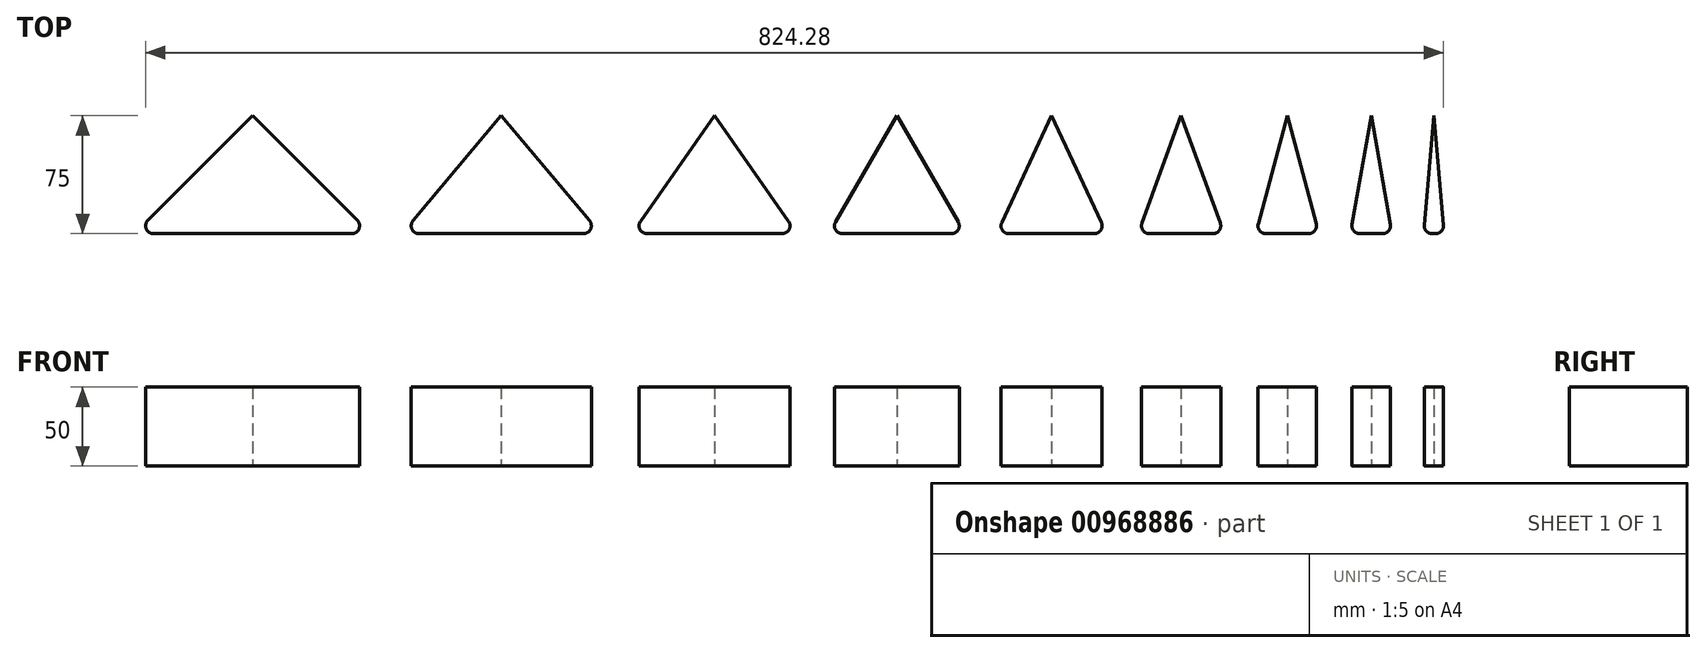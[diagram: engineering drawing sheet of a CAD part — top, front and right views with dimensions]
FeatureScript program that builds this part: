
annotation { "Feature Type Name" : "Feature", "Feature Type Description" : "" }
export const myFeature = defineFeature(function(context is Context, id is Id, definition is map)
    precondition{}
    {
        {
            var Q0;
            Q0=qCreatedBy(makeId("Top.planeOp"),FACE);
            var sketch = newSketch(context, id + "F0", { "sketchPlane" : qUnion([Q0])});
            skLineSegment(sketch, "E0", {"start": v(-473.41, 0) * mm, "end": v(499.22, 0) * mm});
            skLineSegment(sketch, "E1", {"start": v(-389.99, 0) * mm, "end": v(-389.99, 75) * mm});
            skLineSegment(sketch, "E2", {"start": v(-389.99, 75) * mm, "end": v(-464.99, 0) * mm});
            skLineSegment(sketch, "E3.MirrorCS", {"start": v(-389.99, 75) * mm, "end": v(-314.99, 0) * mm});
            skLineSegment(sketch, "E4", {"start": v(-473.41, 0) * mm, "end": v(-473.41, 75) * mm});
            skLineSegment(sketch, "E5", {"start": v(-473.41, 75) * mm, "end": v(499.22, 75) * mm});
            skLineSegment(sketch, "E6", {"start": v(499.22, 75) * mm, "end": v(499.22, 0) * mm});
            skLineSegment(sketch, "E7", {"start": v(-294.99, 0) * mm, "end": v(-232.05, 75) * mm});
            skLineSegment(sketch, "E8", {"start": v(-232.05, 75) * mm, "end": v(-232.05, 0) * mm});
            skLineSegment(sketch, "E9.MirrorCS", {"start": v(-169.12, 0) * mm, "end": v(-232.05, 75) * mm});
            skLineSegment(sketch, "E10", {"start": v(-149.12, 0) * mm, "end": v(-96.6, 75) * mm});
            skLineSegment(sketch, "E11", {"start": v(-96.6, 75) * mm, "end": v(-96.6, 0) * mm});
            skLineSegment(sketch, "E12", {"start": v(-314.99, 0) * mm, "end": v(-294.99, 0) * mm});
            skLineSegment(sketch, "E13", {"start": v(-169.12, 0) * mm, "end": v(-149.12, 0) * mm});
            skLineSegment(sketch, "E14.MirrorCS", {"start": v(-44.1, 0) * mm, "end": v(-96.6, 75) * mm});
            skLineSegment(sketch, "E15", {"start": v(-44.1, 0) * mm, "end": v(-24.1, 0) * mm});
            skLineSegment(sketch, "E16", {"start": v(-24.1, 0) * mm, "end": v(19.21, 75) * mm});
            skLineSegment(sketch, "E17", {"start": v(19.21, 75) * mm, "end": v(19.21, 0) * mm});
            skLineSegment(sketch, "E18.MirrorCS", {"start": v(62.51, 0) * mm, "end": v(19.21, 75) * mm});
            skLineSegment(sketch, "E19", {"start": v(62.51, 0) * mm, "end": v(82.51, 0) * mm});
            skLineSegment(sketch, "E20", {"start": v(82.51, 0) * mm, "end": v(117.49, 75) * mm});
            skLineSegment(sketch, "E21", {"start": v(117.49, 75) * mm, "end": v(117.49, 0) * mm});
            skLineSegment(sketch, "E22.MirrorCS", {"start": v(152.46, 0) * mm, "end": v(117.49, 75) * mm});
            skLineSegment(sketch, "E23", {"start": v(152.46, 0) * mm, "end": v(172.46, 0) * mm});
            skLineSegment(sketch, "E24", {"start": v(172.46, 0) * mm, "end": v(199.76, 75) * mm});
            skLineSegment(sketch, "E25", {"start": v(199.76, 75) * mm, "end": v(199.76, 0) * mm});
            skLineSegment(sketch, "E26.MirrorCS", {"start": v(227.05, 0) * mm, "end": v(199.76, 75) * mm});
            skLineSegment(sketch, "E27", {"start": v(227.05, 0) * mm, "end": v(247.05, 0) * mm});
            skLineSegment(sketch, "E28", {"start": v(247.05, 0) * mm, "end": v(267.15, 75) * mm});
            skLineSegment(sketch, "E29", {"start": v(267.15, 75) * mm, "end": v(267.15, 0) * mm});
            skLineSegment(sketch, "E30.MirrorCS", {"start": v(287.25, 0) * mm, "end": v(267.15, 75) * mm});
            skLineSegment(sketch, "E31", {"start": v(307.25, 0) * mm, "end": v(320.47, 75) * mm});
            skLineSegment(sketch, "E32", {"start": v(320.47, 75) * mm, "end": v(320.47, 0) * mm});
            skLineSegment(sketch, "E33", {"start": v(287.25, 0) * mm, "end": v(307.25, 0) * mm});
            skLineSegment(sketch, "E34.MirrorCS", {"start": v(333.7, 0) * mm, "end": v(320.47, 75) * mm});
            skLineSegment(sketch, "E35", {"start": v(353.7, 0) * mm, "end": v(360.26, 75) * mm});
            skLineSegment(sketch, "E36", {"start": v(360.26, 75) * mm, "end": v(360.26, 0) * mm});
            skLineSegment(sketch, "E37", {"start": v(333.7, 0) * mm, "end": v(353.7, 0) * mm});
            skLineSegment(sketch, "E38.MirrorCS", {"start": v(366.82, 0) * mm, "end": v(360.26, 75) * mm});
            skSolve(sketch);
        }
        {
            var Q0;
            {var subQ0=sQuery(id+"F0.wireOp",EDGE,"E1");Q0=makeQuery(id+"F0.imprint","IMPRINT",FACE,{"disambiguationData":[TD([[makeQuery(id+"F0.imprint","IMPRINT",EDGE,{"derivedFrom":subQ0}),1.0]])]});}
            var Q1;
            {var subQ0=sQuery(id+"F0.wireOp",EDGE,"E1");Q1=makeQuery(id+"F0.imprint","IMPRINT",FACE,{"disambiguationData":[TD([[makeQuery(id+"F0.imprint","IMPRINT",EDGE,{"derivedFrom":subQ0}),-1.0]])]});}
            var Q2;
            {var subQ0=sQuery(id+"F0.wireOp",EDGE,"E7");Q2=makeQuery(id+"F0.imprint","IMPRINT",FACE,{"disambiguationData":[TD([[makeQuery(id+"F0.imprint","IMPRINT",EDGE,{"derivedFrom":subQ0}),-1.0]])]});}
            var Q3;
            {var subQ0=sQuery(id+"F0.wireOp",EDGE,"E8");Q3=makeQuery(id+"F0.imprint","IMPRINT",FACE,{"disambiguationData":[TD([[makeQuery(id+"F0.imprint","IMPRINT",EDGE,{"derivedFrom":subQ0}),1.0]])]});}
            var Q4;
            {var subQ0=sQuery(id+"F0.wireOp",EDGE,"E11");Q4=makeQuery(id+"F0.imprint","IMPRINT",FACE,{"disambiguationData":[TD([[makeQuery(id+"F0.imprint","IMPRINT",EDGE,{"derivedFrom":subQ0}),1.0]])]});}
            var Q5;
            {var subQ0=sQuery(id+"F0.wireOp",EDGE,"E10");Q5=makeQuery(id+"F0.imprint","IMPRINT",FACE,{"disambiguationData":[TD([[makeQuery(id+"F0.imprint","IMPRINT",EDGE,{"derivedFrom":subQ0}),-1.0]])]});}
            var Q6;
            {var subQ0=sQuery(id+"F0.wireOp",EDGE,"E16");Q6=makeQuery(id+"F0.imprint","IMPRINT",FACE,{"disambiguationData":[TD([[makeQuery(id+"F0.imprint","IMPRINT",EDGE,{"derivedFrom":subQ0}),-1.0]])]});}
            var Q7;
            {var subQ0=sQuery(id+"F0.wireOp",EDGE,"E17");Q7=makeQuery(id+"F0.imprint","IMPRINT",FACE,{"disambiguationData":[TD([[makeQuery(id+"F0.imprint","IMPRINT",EDGE,{"derivedFrom":subQ0}),1.0]])]});}
            var Q8;
            {var subQ0=sQuery(id+"F0.wireOp",EDGE,"E20");Q8=makeQuery(id+"F0.imprint","IMPRINT",FACE,{"disambiguationData":[TD([[makeQuery(id+"F0.imprint","IMPRINT",EDGE,{"derivedFrom":subQ0}),-1.0]])]});}
            var Q9;
            {var subQ0=sQuery(id+"F0.wireOp",EDGE,"E21");Q9=makeQuery(id+"F0.imprint","IMPRINT",FACE,{"disambiguationData":[TD([[makeQuery(id+"F0.imprint","IMPRINT",EDGE,{"derivedFrom":subQ0}),1.0]])]});}
            var Q10;
            {var subQ0=sQuery(id+"F0.wireOp",EDGE,"E25");Q10=makeQuery(id+"F0.imprint","IMPRINT",FACE,{"disambiguationData":[TD([[makeQuery(id+"F0.imprint","IMPRINT",EDGE,{"derivedFrom":subQ0}),1.0]])]});}
            var Q11;
            {var subQ0=sQuery(id+"F0.wireOp",EDGE,"E24");Q11=makeQuery(id+"F0.imprint","IMPRINT",FACE,{"disambiguationData":[TD([[makeQuery(id+"F0.imprint","IMPRINT",EDGE,{"derivedFrom":subQ0}),-1.0]])]});}
            var Q12;
            {var subQ0=sQuery(id+"F0.wireOp",EDGE,"E29");Q12=makeQuery(id+"F0.imprint","IMPRINT",FACE,{"disambiguationData":[TD([[makeQuery(id+"F0.imprint","IMPRINT",EDGE,{"derivedFrom":subQ0}),1.0]])]});}
            var Q13;
            {var subQ0=sQuery(id+"F0.wireOp",EDGE,"E32");Q13=makeQuery(id+"F0.imprint","IMPRINT",FACE,{"disambiguationData":[TD([[makeQuery(id+"F0.imprint","IMPRINT",EDGE,{"derivedFrom":subQ0}),1.0]])]});}
            var Q14;
            {var subQ0=sQuery(id+"F0.wireOp",EDGE,"E31");Q14=makeQuery(id+"F0.imprint","IMPRINT",FACE,{"disambiguationData":[TD([[makeQuery(id+"F0.imprint","IMPRINT",EDGE,{"derivedFrom":subQ0}),-1.0]])]});}
            var Q15;
            {var subQ0=sQuery(id+"F0.wireOp",EDGE,"E35");Q15=makeQuery(id+"F0.imprint","IMPRINT",FACE,{"disambiguationData":[TD([[makeQuery(id+"F0.imprint","IMPRINT",EDGE,{"derivedFrom":subQ0}),-1.0]])]});}
            var Q16;
            {var subQ2=sQuery(id+"F0.wireOp",EDGE,"E36");Q16=makeQuery(id+"F0.imprint","IMPRINT",FACE,{"disambiguationData":[TD([[makeQuery(id+"F0.imprint","IMPRINT",EDGE,{"derivedFrom":subQ2}),1.0]])]});}
            var Q17;
            {var subQ0=sQuery(id+"F0.wireOp",EDGE,"E28");Q17=makeQuery(id+"F0.imprint","IMPRINT",FACE,{"disambiguationData":[TD([[makeQuery(id+"F0.imprint","IMPRINT",EDGE,{"derivedFrom":subQ0}),-1.0]])]});}
            extrude(context, id + "F1", {"entities" : qUnion([Q0, Q1, Q2, Q3, Q4, Q5, Q6, Q7, Q8, Q9, Q10, Q11, Q12, Q13, Q14, Q15, Q16, Q17]), "depth" : 50 * mm, "offsetDistance" : 25 * mm});
        }
        {
            var Q0;
            Q0=makeQuery(id+"F1.opExtrude","SWEPT_EDGE",EDGE,{"disambiguationData":[OSD([sQuery(id+"F0.wireOp",EDGE,"E0"),sQuery(id+"F0.wireOp",EDGE,"E2")])]});
            var Q1;
            Q1=makeQuery(id+"F1.opExtrude","SWEPT_EDGE",EDGE,{"disambiguationData":[OSD([sQuery(id+"F0.wireOp",EDGE,"E0"),sQuery(id+"F0.wireOp",EDGE,"E3.MirrorCS")])]});
            var Q2;
            Q2=makeQuery(id+"F1.opExtrude","SWEPT_EDGE",EDGE,{"disambiguationData":[OSD([sQuery(id+"F0.wireOp",EDGE,"E0"),sQuery(id+"F0.wireOp",EDGE,"E7")])]});
            var Q3;
            Q3=makeQuery(id+"F1.opExtrude","SWEPT_EDGE",EDGE,{"disambiguationData":[OSD([sQuery(id+"F0.wireOp",EDGE,"E0"),sQuery(id+"F0.wireOp",EDGE,"E9.MirrorCS")])]});
            var Q4;
            Q4=makeQuery(id+"F1.opExtrude","SWEPT_EDGE",EDGE,{"disambiguationData":[OSD([sQuery(id+"F0.wireOp",EDGE,"E0"),sQuery(id+"F0.wireOp",EDGE,"E10")])]});
            var Q5;
            Q5=makeQuery(id+"F1.opExtrude","SWEPT_EDGE",EDGE,{"disambiguationData":[OSD([sQuery(id+"F0.wireOp",EDGE,"E0"),sQuery(id+"F0.wireOp",EDGE,"E14.MirrorCS")])]});
            var Q6;
            Q6=makeQuery(id+"F1.opExtrude","SWEPT_EDGE",EDGE,{"disambiguationData":[OSD([sQuery(id+"F0.wireOp",EDGE,"E0"),sQuery(id+"F0.wireOp",EDGE,"E16")])]});
            var Q7;
            Q7=makeQuery(id+"F1.opExtrude","SWEPT_EDGE",EDGE,{"disambiguationData":[OSD([sQuery(id+"F0.wireOp",EDGE,"E0"),sQuery(id+"F0.wireOp",EDGE,"E18.MirrorCS")])]});
            var Q8;
            Q8=makeQuery(id+"F1.opExtrude","SWEPT_EDGE",EDGE,{"disambiguationData":[OSD([sQuery(id+"F0.wireOp",EDGE,"E0"),sQuery(id+"F0.wireOp",EDGE,"E20")])]});
            var Q9;
            Q9=makeQuery(id+"F1.opExtrude","SWEPT_EDGE",EDGE,{"disambiguationData":[OSD([sQuery(id+"F0.wireOp",EDGE,"E0"),sQuery(id+"F0.wireOp",EDGE,"E22.MirrorCS")])]});
            var Q10;
            Q10=makeQuery(id+"F1.opExtrude","SWEPT_EDGE",EDGE,{"disambiguationData":[OSD([sQuery(id+"F0.wireOp",EDGE,"E0"),sQuery(id+"F0.wireOp",EDGE,"E24")])]});
            var Q11;
            Q11=makeQuery(id+"F1.opExtrude","SWEPT_EDGE",EDGE,{"disambiguationData":[OSD([sQuery(id+"F0.wireOp",EDGE,"E0"),sQuery(id+"F0.wireOp",EDGE,"E26.MirrorCS")])]});
            var Q12;
            Q12=makeQuery(id+"F1.opExtrude","SWEPT_EDGE",EDGE,{"disambiguationData":[OSD([sQuery(id+"F0.wireOp",EDGE,"E0"),sQuery(id+"F0.wireOp",EDGE,"E28")])]});
            var Q13;
            Q13=makeQuery(id+"F1.opExtrude","SWEPT_EDGE",EDGE,{"disambiguationData":[OSD([sQuery(id+"F0.wireOp",EDGE,"E0"),sQuery(id+"F0.wireOp",EDGE,"E30.MirrorCS")])]});
            var Q14;
            Q14=makeQuery(id+"F1.opExtrude","SWEPT_EDGE",EDGE,{"disambiguationData":[OSD([sQuery(id+"F0.wireOp",EDGE,"E0"),sQuery(id+"F0.wireOp",EDGE,"E31")])]});
            var Q15;
            Q15=makeQuery(id+"F1.opExtrude","SWEPT_EDGE",EDGE,{"disambiguationData":[OSD([sQuery(id+"F0.wireOp",EDGE,"E0"),sQuery(id+"F0.wireOp",EDGE,"E34.MirrorCS")])]});
            var Q16;
            Q16=makeQuery(id+"F1.opExtrude","SWEPT_EDGE",EDGE,{"disambiguationData":[OSD([sQuery(id+"F0.wireOp",EDGE,"E0"),sQuery(id+"F0.wireOp",EDGE,"E35")])]});
            var Q17;
            Q17=makeQuery(id+"F1.opExtrude","SWEPT_EDGE",EDGE,{"disambiguationData":[OSD([sQuery(id+"F0.wireOp",EDGE,"E0"),sQuery(id+"F0.wireOp",EDGE,"E38.MirrorCS")])]});
            fillet(context, id + "F2", {"entities" : qUnion([Q0, Q1, Q2, Q3, Q4, Q5, Q6, Q7, Q8, Q9, Q10, Q11, Q12, Q13, Q14, Q15, Q16, Q17]), "tangentPropagation" : true, "radius" : 5 * mm, "defaultsChanged" : false, "vertexSettings" : [], "allowEdgeOverflow" : false});
        }
    });
